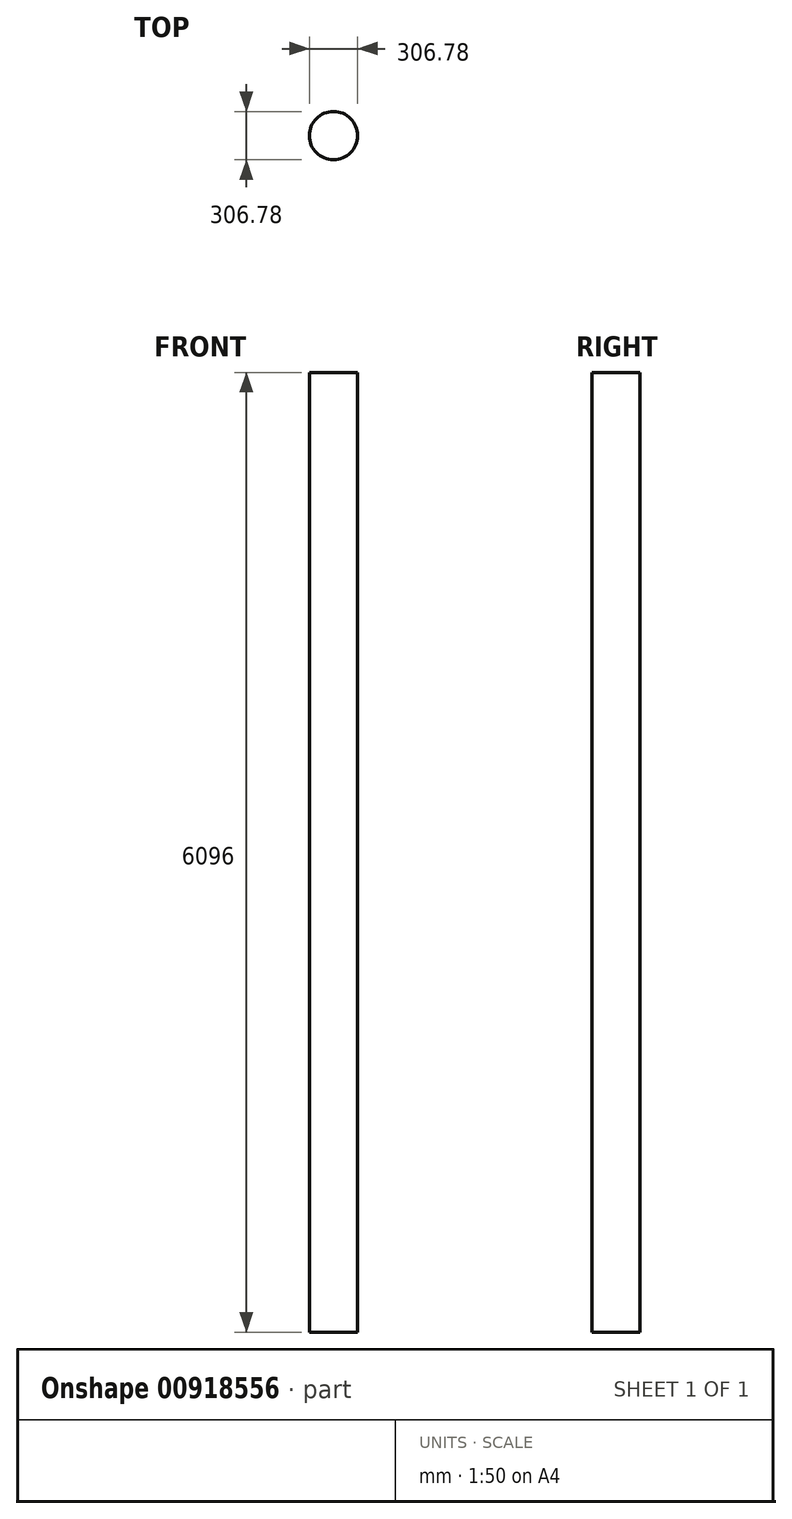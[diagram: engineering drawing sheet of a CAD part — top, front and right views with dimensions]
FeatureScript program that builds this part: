
annotation { "Feature Type Name" : "Feature", "Feature Type Description" : "" }
export const myFeature = defineFeature(function(context is Context, id is Id, definition is map)
    precondition{}
    {
        {
            var Q0;
            Q0=qCreatedBy(makeId("Top.planeOp"),FACE);
            var sketch = newSketch(context, id + "F0", { "sketchPlane" : qUnion([Q0])});
            skCircle(sketch, "E0", {"center": v(0, 0) * mm, "radius": 153.4 * mm});
            skSolve(sketch);
        }
        {
            var Q0;
            Q0=makeQuery(id+"F0.imprint","IMPRINT",FACE,{"disambiguationData":[TD([[makeQuery(id+"F0.imprint","IMPRINT",EDGE,{"derivedFrom":sQuery(id+"F0.wireOp",EDGE,"E0")}),1.0]])]});
            extrude(context, id + "F1", {"entities" : qUnion([Q0]), "depth" : 6096 * mm, "offsetDistance" : 30.48 * mm});
        }
    });
